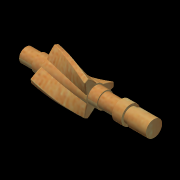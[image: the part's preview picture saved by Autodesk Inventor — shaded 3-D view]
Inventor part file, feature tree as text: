
AUTODESK INVENTOR PART (.ipt)
format: ipt  version: 2020 (Build 240168000, 168)  size: 416,256 bytes
history: native  units: mm
features: extrude x4, fillet x2, other x1, revolve x1, mirror x1, chamfer x1, helix x1, pattern_circular x1
ambient origin geometry x8: Origin, YZ Plane, XZ Plane, XY Plane, X Axis, Y Axis, Z Axis, Center Point
bodies: Body1 (feature_tree)
feature tree (12):
  other  "實體1"
  revolve  "Revolution1"  [1 undecoded]
  mirror  "Mirror1"
  extrude  "Extrusion5"  Depth=5.0mm
  extrude  "Extrusion6"  Depth=1.75mm
  chamfer  "Chamfer4"  Distance=1.5mm
  extrude  "Extrusion8"  Depth=3.0mm
  extrude  "Extrusion9"  TaperAngle=90.0deg  [1 undecoded]
  helix  "Coil4"  [1 undecoded]
  pattern_circular  "Circular Pattern3"  [2 undecoded]
  fillet  "Fillet6"  Radius=4.0mm
  fillet  "Fillet7"  Radius=2.0mm
note: 5 required parameter values undecoded (feature->parameter linkage not recoverable at this tier; creation-order binding heuristic only, values carry confidence <= 0.55)